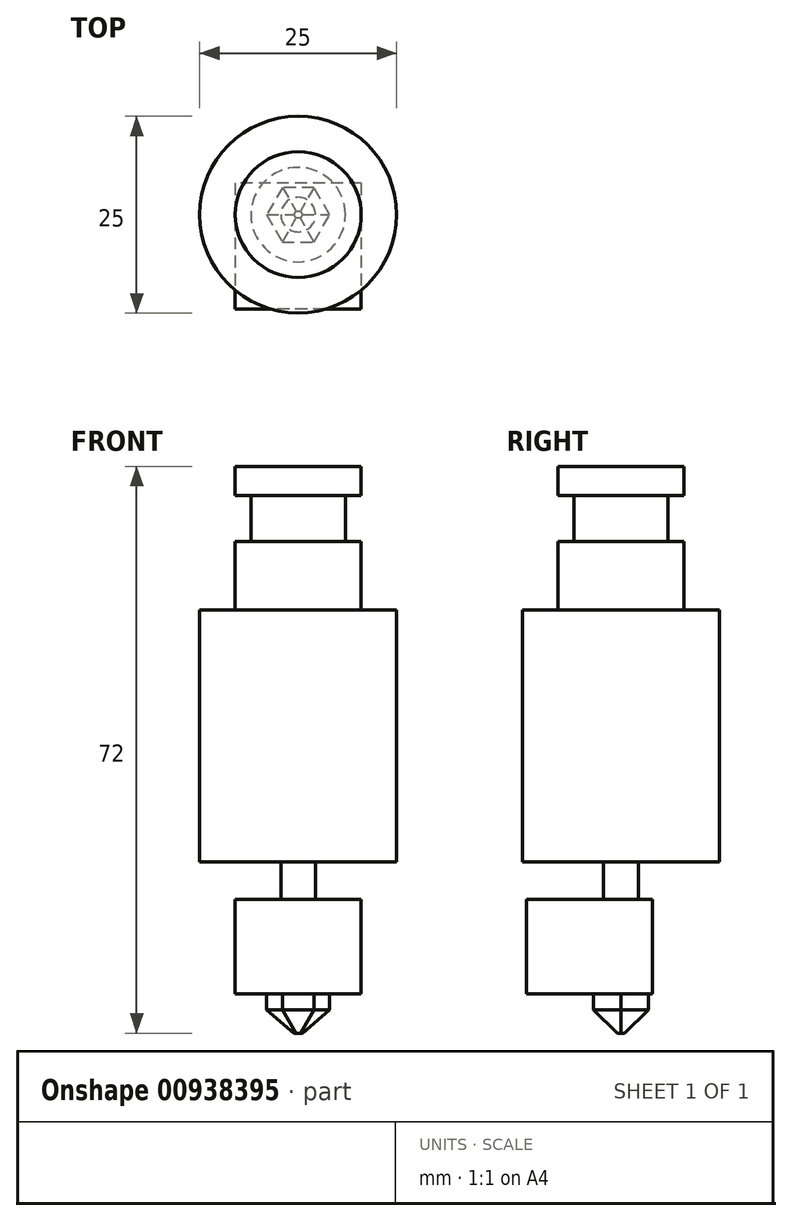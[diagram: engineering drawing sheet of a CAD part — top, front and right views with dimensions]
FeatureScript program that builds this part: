
annotation { "Feature Type Name" : "Feature", "Feature Type Description" : "" }
export const myFeature = defineFeature(function(context is Context, id is Id, definition is map)
    precondition{}
    {
        {
            var Q0;
            Q0=qCreatedBy(makeId("Top.planeOp"),FACE);
            var sketch = newSketch(context, id + "F0", { "sketchPlane" : qUnion([Q0])});
            skCircle(sketch, "E0", {"center": v(0, 0) * mm, "radius": 8 * mm});
            skSolve(sketch);
        }
        {
            var Q0;
            Q0=qSketchRegion(id+"F0",true);
            extrude(context, id + "F1", {"entities" : qUnion([Q0]), "depth" : 3.7 * mm});
        }
        {
            var Q0;
            Q0=makeQuery(id+"F1.opExtrude","CAP_FACE",FACE,{"disambiguationData":[OSD([sQuery(id+"F0.wireOp",EDGE,"E0")])],"isStart":true});
            var sketch = newSketch(context, id + "F2", { "sketchPlane" : qUnion([Q0])});
            skCircle(sketch, "E1", {"center": v(0, 0) * mm, "radius": 6 * mm});
            skSolve(sketch);
        }
        {
            var Q0;
            Q0=qSketchRegion(id+"F2",true);
            extrude(context, id + "F3", {"entities" : qUnion([Q0]), "operationType" : NewBodyOperationType.ADD, "depth" : 5.8 * mm, "offsetDistance" : 25 * mm});
        }
        {
            var Q0;
            Q0=makeQuery(id+"F3.opExtrude","CAP_FACE",FACE,{"disambiguationData":[OSD([sQuery(id+"F2.wireOp",EDGE,"E1")])],"isStart":false});
            var sketch = newSketch(context, id + "F4", { "sketchPlane" : qUnion([Q0])});
            skCircle(sketch, "E2", {"center": v(0, 0) * mm, "radius": 8 * mm});
            skSolve(sketch);
        }
        {
            var Q0;
            Q0=qSketchRegion(id+"F4",true);
            extrude(context, id + "F5", {"entities" : qUnion([Q0]), "operationType" : NewBodyOperationType.ADD, "depth" : 8.7 * mm, "offsetDistance" : 25 * mm});
        }
        {
            var Q0;
            Q0=makeQuery(id+"F5.opExtrude","CAP_FACE",FACE,{"disambiguationData":[OSD([sQuery(id+"F4.wireOp",EDGE,"E2")])],"isStart":false});
            var sketch = newSketch(context, id + "F6", { "sketchPlane" : qUnion([Q0])});
            skCircle(sketch, "E3", {"center": v(0, 0) * mm, "radius": 12.5 * mm});
            skSolve(sketch);
        }
        {
            var Q0;
            Q0=qSketchRegion(id+"F6",true);
            extrude(context, id + "F7", {"entities" : qUnion([Q0]), "operationType" : NewBodyOperationType.ADD, "depth" : 32 * mm, "offsetDistance" : 25 * mm});
        }
        {
            var Q0;
            Q0=makeQuery(id+"F7.opExtrude","CAP_FACE",FACE,{"disambiguationData":[OSD([sQuery(id+"F6.wireOp",EDGE,"E3")])],"isStart":false});
            var sketch = newSketch(context, id + "F8", { "sketchPlane" : qUnion([Q0])});
            skCircle(sketch, "E4", {"center": v(0, 0) * mm, "radius": 2.2 * mm});
            skSolve(sketch);
        }
        {
            var Q0;
            Q0=makeQuery(id+"F8.imprint","IMPRINT",FACE,{"disambiguationData":[TD([[makeQuery(id+"F8.imprint","IMPRINT",EDGE,{"derivedFrom":sQuery(id+"F8.wireOp",EDGE,"E4")}),1.0]])]});
            extrude(context, id + "F9", {"entities" : qUnion([Q0]), "operationType" : NewBodyOperationType.ADD, "depth" : 4.8 * mm, "offsetDistance" : 25 * mm});
        }
        {
            var Q0;
            Q0=makeQuery(id+"F9.opExtrude","CAP_FACE",FACE,{"disambiguationData":[OSD([sQuery(id+"F8.wireOp",EDGE,"E4")])],"isStart":false});
            var sketch = newSketch(context, id + "F10", { "sketchPlane" : qUnion([Q0])});
            skLineSegment(sketch, "E5.bottom", {"start": v(8, -4) * mm, "end": v(-8, -4) * mm});
            skLineSegment(sketch, "E5.top", {"start": v(8, 12) * mm, "end": v(-8, 12) * mm});
            skLineSegment(sketch, "E5.left", {"start": v(8, -4) * mm, "end": v(8, 12) * mm});
            skLineSegment(sketch, "E5.right", {"start": v(-8, -4) * mm, "end": v(-8, 12) * mm});
            skPoint(sketch, "E6", {"position": v(0, 0) * mm});
            skSolve(sketch);
        }
        {
            var Q0;
            Q0 = qSketchRegion(id + "F10", true);
            extrude(context, id + "F11", {"entities" : qUnion([Q0]), "operationType" : NewBodyOperationType.ADD, "depth" : 12 * mm, "offsetDistance" : 25 * mm});
        }
        {
            var Q0;
            Q0=makeQuery(id+"F11.opExtrude","CAP_FACE",FACE,{"disambiguationData":[OSD([sQuery(id+"F10.wireOp",EDGE,"E5.bottom"),sQuery(id+"F10.wireOp",EDGE,"E5.top"),sQuery(id+"F10.wireOp",EDGE,"E5.left"),sQuery(id+"F10.wireOp",EDGE,"E5.right")])],"isStart":false});
            var sketch = newSketch(context, id + "F12", { "sketchPlane" : qUnion([Q0])});
            skCircle(sketch, "E7.cCircle", {"center": v(0, 0) * mm, "radius": 3.46 * mm, "construction": true});
            skLineSegment(sketch, "E7.0", {"start": v(-2, 3.46) * mm, "end": v(2, 3.46) * mm});
            skLineSegment(sketch, "E7.1", {"start": v(2, 3.46) * mm, "end": v(4, 0) * mm});
            skLineSegment(sketch, "E7.2", {"start": v(4, 0) * mm, "end": v(2, -3.46) * mm});
            skLineSegment(sketch, "E7.3", {"start": v(2, -3.46) * mm, "end": v(-2, -3.46) * mm});
            skLineSegment(sketch, "E7.4", {"start": v(-2, -3.46) * mm, "end": v(-4, 0) * mm});
            skLineSegment(sketch, "E7.5", {"start": v(-4, 0) * mm, "end": v(-2, 3.46) * mm});
            skPoint(sketch, "E7.0.midPoint", {"position": v(0, 3.46) * mm});
            skSolve(sketch);
        }
        {
            var Q0;
            Q0=makeQuery(id+"F12.imprint","IMPRINT",FACE,{"disambiguationData":[TD([[makeQuery(id+"F12.imprint","IMPRINT",EDGE,{"derivedFrom":sQuery(id+"F12.wireOp",EDGE,"E7.0")}),-1.0]])]});
            extrude(context, id + "F13", {"entities" : qUnion([Q0]), "operationType" : NewBodyOperationType.ADD, "depth" : 5 * mm, "offsetDistance" : 25 * mm});
        }
        {
            var Q0;
            Q0=makeQuery(id+"F13.opExtrude","CAP_EDGE",EDGE,{"disambiguationData":[OSD([sQuery(id+"F12.wireOp",EDGE,"E7.0")])],"isStart":false});
            var Q1;
            Q1=makeQuery(id+"F13.opExtrude","CAP_EDGE",EDGE,{"disambiguationData":[OSD([sQuery(id+"F12.wireOp",EDGE,"E7.5")])],"isStart":false});
            var Q2;
            Q2=makeQuery(id+"F13.opExtrude","CAP_EDGE",EDGE,{"disambiguationData":[OSD([sQuery(id+"F12.wireOp",EDGE,"E7.4")])],"isStart":false});
            var Q3;
            Q3=makeQuery(id+"F13.opExtrude","CAP_EDGE",EDGE,{"disambiguationData":[OSD([sQuery(id+"F12.wireOp",EDGE,"E7.3")])],"isStart":false});
            var Q4;
            Q4=makeQuery(id+"F13.opExtrude","CAP_EDGE",EDGE,{"disambiguationData":[OSD([sQuery(id+"F12.wireOp",EDGE,"E7.2")])],"isStart":false});
            var Q5;
            Q5=makeQuery(id+"F13.opExtrude","CAP_EDGE",EDGE,{"disambiguationData":[OSD([sQuery(id+"F12.wireOp",EDGE,"E7.1")])],"isStart":false});
            chamfer(context, id + "F14", {"entities" : qUnion([Q0, Q1, Q2, Q3, Q4, Q5]), "width" : 3 * mm, "tangentPropagation" : true});
        }
    });
